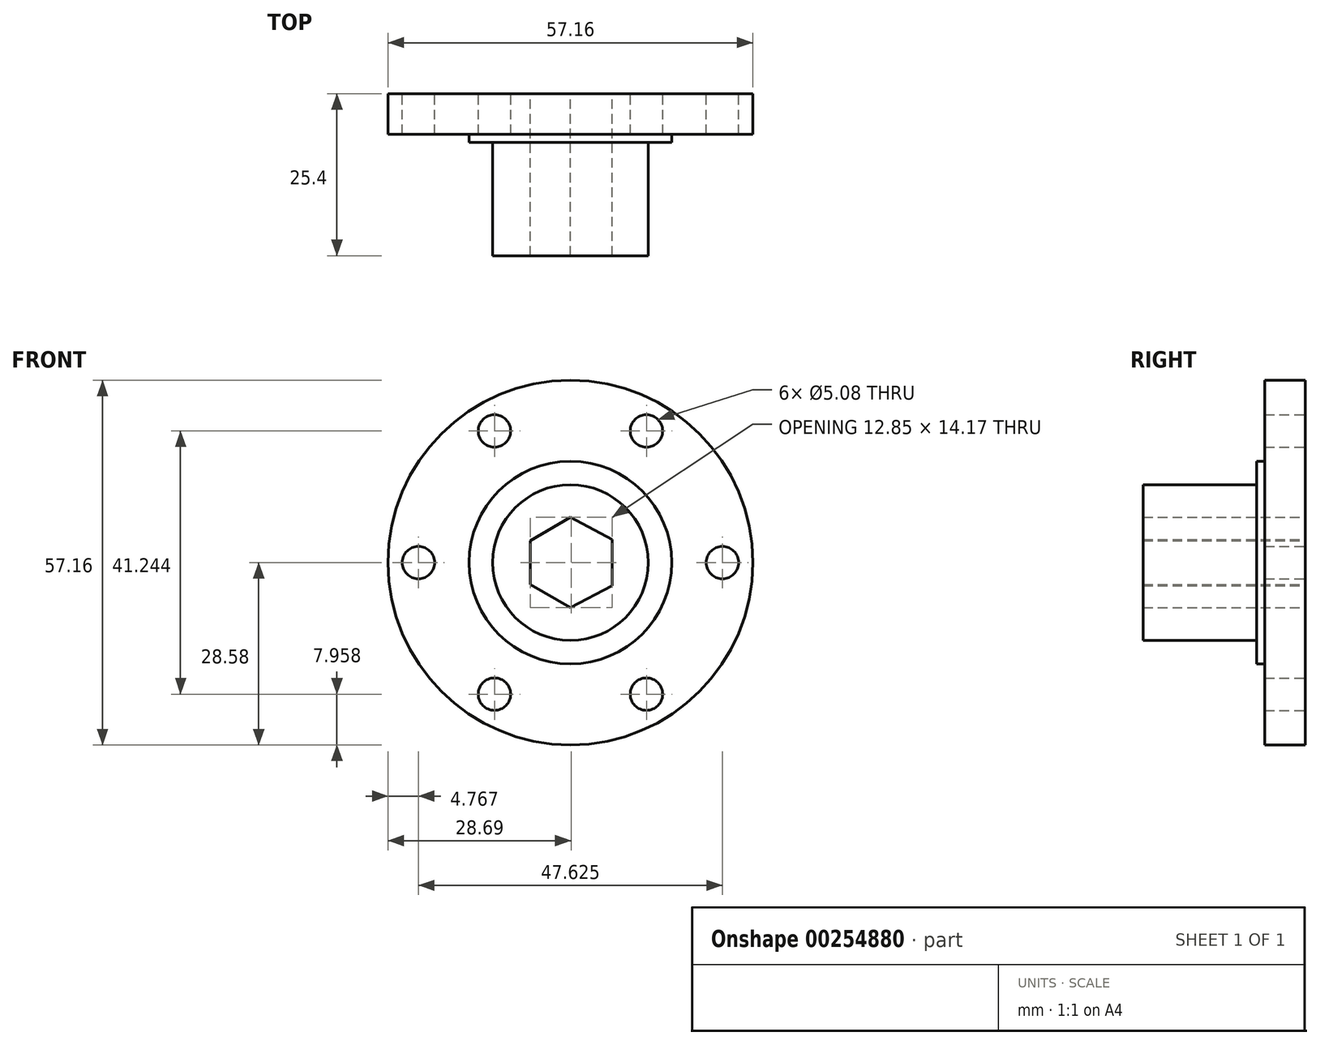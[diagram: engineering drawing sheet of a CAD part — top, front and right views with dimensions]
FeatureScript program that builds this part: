
annotation { "Feature Type Name" : "Feature", "Feature Type Description" : "" }
export const myFeature = defineFeature(function(context is Context, id is Id, definition is map)
    precondition{}
    {
        {
            var Q0;
            Q0=qCreatedBy(makeId("Front.planeOp"),FACE);
            var sketch = newSketch(context, id + "F0", { "sketchPlane" : qUnion([Q0])});
            skLineSegment(sketch, "E0.bottom", {"start": v(28.58, 28.58) * mm, "end": v(-28.58, 28.58) * mm});
            skLineSegment(sketch, "E0.top", {"start": v(28.58, -28.58) * mm, "end": v(-28.58, -28.58) * mm});
            skLineSegment(sketch, "E0.left", {"start": v(28.58, 28.58) * mm, "end": v(28.58, -28.58) * mm});
            skLineSegment(sketch, "E0.right", {"start": v(-28.57, 28.58) * mm, "end": v(-28.58, -28.58) * mm});
            skPoint(sketch, "E0.middle", {"position": v(0, 0) * mm});
            skCircle(sketch, "E1", {"center": v(0, 0) * mm, "radius": 28.58 * mm});
            skCircle(sketch, "E2", {"center": v(-23.81, 0) * mm, "radius": 2.54 * mm});
            skCircle(sketch, "E3", {"center": v(23.81, 0) * mm, "radius": 2.54 * mm});
            skCircle(sketch, "E4.2.0", {"center": v(11.9, -20.62) * mm, "radius": 2.54 * mm});
            skCircle(sketch, "E5.2.0", {"center": v(-11.9, 20.62) * mm, "radius": 2.54 * mm});
            skCircle(sketch, "E6.2.0", {"center": v(-11.9, -20.62) * mm, "radius": 2.54 * mm});
            skCircle(sketch, "E7.2.0", {"center": v(11.9, 20.62) * mm, "radius": 2.54 * mm});
            skCircle(sketch, "E8", {"center": v(0, 0) * mm, "radius": 15.88 * mm});
            skCircle(sketch, "E9", {"center": v(0, 0) * mm, "radius": 12.2 * mm});
            skLineSegment(sketch, "E10.0", {"start": v(6.54, 3.64) * mm, "end": v(6.54, -3.64) * mm});
            skLineSegment(sketch, "E10.1", {"start": v(6.54, -3.64) * mm, "end": v(0, -7.09) * mm});
            skLineSegment(sketch, "E10.2", {"start": v(0, -7.09) * mm, "end": v(-6.32, -3.44) * mm});
            skLineSegment(sketch, "E10.3", {"start": v(-6.32, -3.44) * mm, "end": v(-6.32, 3.44) * mm});
            skLineSegment(sketch, "E10.4", {"start": v(-6.32, 3.44) * mm, "end": v(0, 7.09) * mm});
            skLineSegment(sketch, "E10.5", {"start": v(0, 7.09) * mm, "end": v(6.54, 3.64) * mm});
            skSolve(sketch);
        }
        {
            var Q0;
            Q0=makeQuery(id+"F0.imprint","IMPRINT",FACE,{"disambiguationData":[TD([[makeQuery(id+"F0.imprint","IMPRINT",EDGE,{"derivedFrom":sQuery(id+"F0.wireOp",EDGE,"E2")}),-1.0]])]});
            extrude(context, id + "F1", {"entities" : qUnion([Q0]), "depth" : 6.35 * mm});
        }
        {
            var Q0;
            Q0=makeQuery(id+"F0.imprint","IMPRINT",FACE,{"disambiguationData":[TD([[makeQuery(id+"F0.imprint","IMPRINT",EDGE,{"derivedFrom":sQuery(id+"F0.wireOp",EDGE,"E8")}),1.0]])]});
            extrude(context, id + "F2", {"entities" : qUnion([Q0]), "operationType" : NewBodyOperationType.ADD, "depth" : 7.62 * mm});
        }
        {
            var Q0;
            Q0=makeQuery(id+"F0.imprint","IMPRINT",FACE,{"disambiguationData":[TD([[makeQuery(id+"F0.imprint","IMPRINT",EDGE,{"derivedFrom":sQuery(id+"F0.wireOp",EDGE,"E9")}),1.0]])]});
            extrude(context, id + "F3", {"entities" : qUnion([Q0]), "operationType" : NewBodyOperationType.ADD, "depth" : 25.4 * mm});
        }
    });
